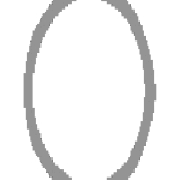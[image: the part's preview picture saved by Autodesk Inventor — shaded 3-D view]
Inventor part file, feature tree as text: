
AUTODESK INVENTOR PART (.ipt)
format: ipt  version: 2021 (Build 250183000, 183)  size: 110,592 bytes
history: native  units: in
note: dims shown in document units (in); Inventor stores cm internally (conversion verified against a paired STEP export)
features: other x4, sketch x3, plane x1
ambient origin geometry x8: Origin, YZ Plane, XZ Plane, XY Plane, X Axis, Y Axis, Z Axis, Center Point
bodies: Solid1 (feature_tree), Body (feature_tree)
feature tree (8):
  other  "Driven Length"
  other  "Frame Generator"
  other  "Start Plane"
  other  "End Plane"
  sketch  "Sketch"  dims[d2=8.0898in d4=-0.0in d5=8.0898in d6=0.12in d7=0.0in d8=90.0deg d9=8.0898in]
  sketch  "Sketch2"  dims[d0=1.0in]
  plane  "Work Plane3"
  sketch  "Sketch3"  dims[d1=0.065in]
